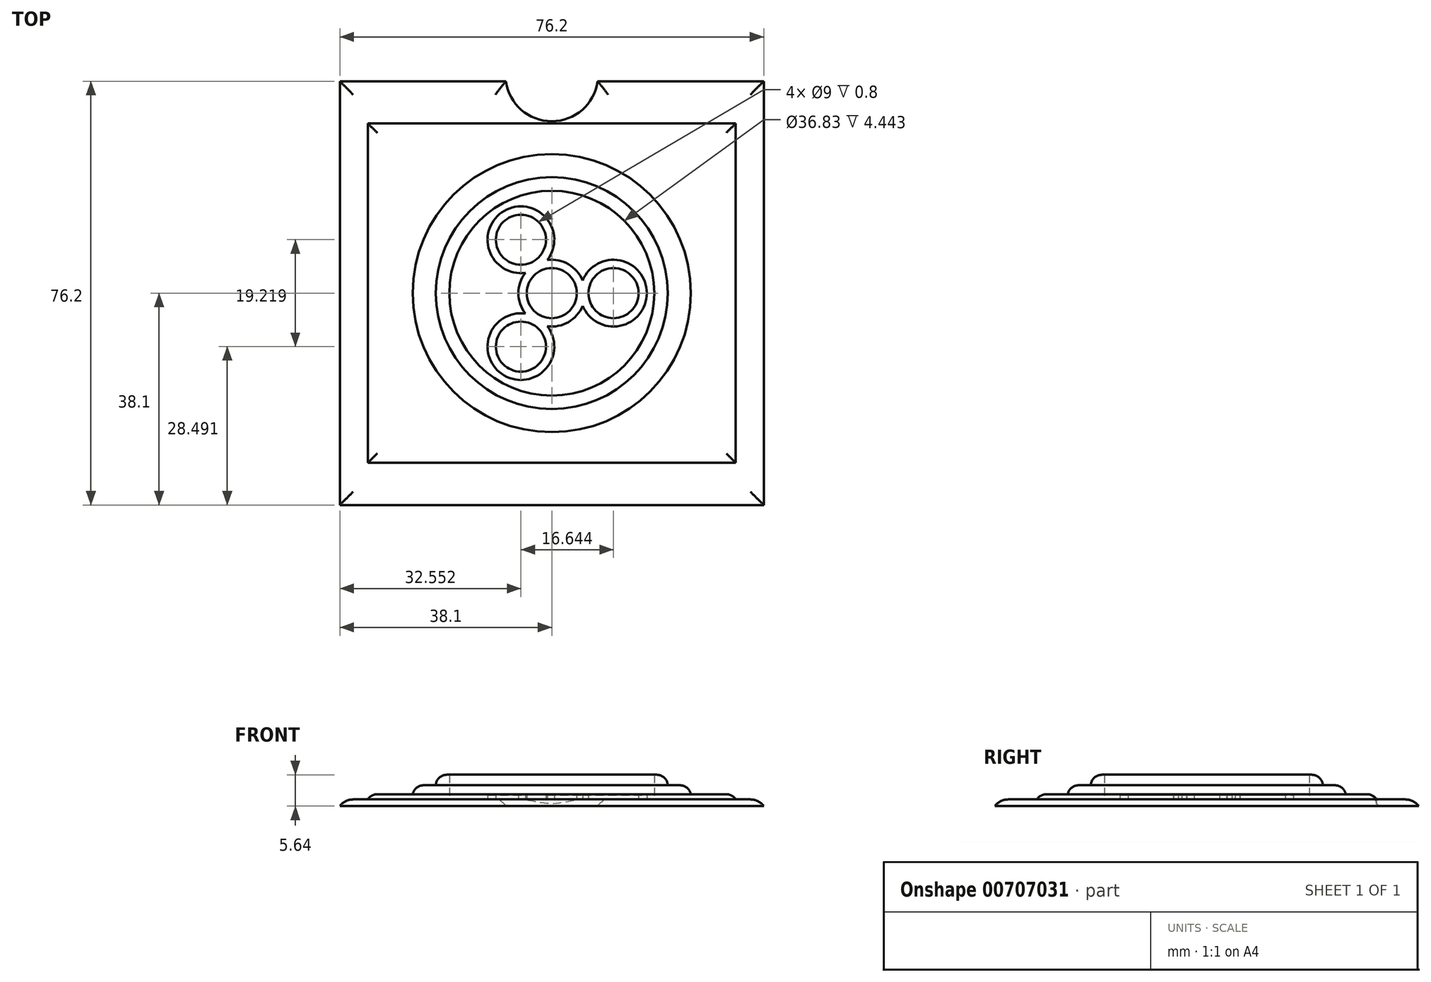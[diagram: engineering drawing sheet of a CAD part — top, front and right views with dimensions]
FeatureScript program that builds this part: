
annotation { "Feature Type Name" : "Feature", "Feature Type Description" : "" }
export const myFeature = defineFeature(function(context is Context, id is Id, definition is map)
    precondition{}
    {
        {
            var Q0;
            Q0=qCreatedBy(makeId("Top.planeOp"),FACE);
            var sketch = newSketch(context, id + "F0", { "sketchPlane" : qUnion([Q0])});
            skLineSegment(sketch, "E0.bottom", {"start": v(38.1, 38.1) * mm, "end": v(-38.1, 38.1) * mm});
            skLineSegment(sketch, "E0.top", {"start": v(38.1, -38.1) * mm, "end": v(-38.1, -38.1) * mm});
            skLineSegment(sketch, "E0.left", {"start": v(38.1, 38.1) * mm, "end": v(38.1, -38.1) * mm});
            skLineSegment(sketch, "E0.right", {"start": v(-38.1, 38.1) * mm, "end": v(-38.1, -38.1) * mm});
            skPoint(sketch, "E0.middle", {"position": v(0, 0) * mm});
            skSolve(sketch);
        }
        {
            var Q0;
            Q0=makeQuery(id+"F0.imprint","IMPRINT",FACE,{"disambiguationData":[TD([[makeQuery(id+"F0.imprint","IMPRINT",EDGE,{"derivedFrom":sQuery(id+"F0.wireOp",EDGE,"E0.bottom")}),1.0]])]});
            extrude(context, id + "F1", {"entities" : qUnion([Q0]), "depth" : 1.2 * mm, "offsetDistance" : 25 * mm});
        }
        {
            var Q0;
            Q0=qCreatedBy(makeId("Top.planeOp"),FACE);
            var sketch = newSketch(context, id + "F2", { "sketchPlane" : qUnion([Q0])});
            skLineSegment(sketch, "E1.bottom", {"start": v(33.07, 30.52) * mm, "end": v(-33.07, 30.52) * mm});
            skLineSegment(sketch, "E1.top", {"start": v(33.07, -30.52) * mm, "end": v(-33.07, -30.52) * mm});
            skLineSegment(sketch, "E1.left", {"start": v(33.07, 30.52) * mm, "end": v(33.07, -30.52) * mm});
            skLineSegment(sketch, "E1.right", {"start": v(-33.07, 30.52) * mm, "end": v(-33.07, -30.52) * mm});
            skPoint(sketch, "E1.middle", {"position": v(0, 0) * mm});
            skSolve(sketch);
        }
        {
            var Q0;
            Q0=makeQuery(id+"F2.imprint","IMPRINT",FACE,{"disambiguationData":[TD([[makeQuery(id+"F2.imprint","IMPRINT",EDGE,{"derivedFrom":sQuery(id+"F2.wireOp",EDGE,"E1.bottom")}),1.0]])]});
            extrude(context, id + "F3", {"entities" : qUnion([Q0]), "operationType" : NewBodyOperationType.ADD, "depth" : 2.14 * mm, "offsetDistance" : 25 * mm});
        }
        {
            var Q0;
            Q0=qCreatedBy(makeId("Top.planeOp"),FACE);
            var sketch = newSketch(context, id + "F4", { "sketchPlane" : qUnion([Q0])});
            skCircle(sketch, "E2", {"center": v(0, 0) * mm, "radius": 25 * mm});
            skSolve(sketch);
        }
        {
            var Q0;
            Q0=makeQuery(id+"F4.imprint","IMPRINT",FACE,{"disambiguationData":[TD([[makeQuery(id+"F4.imprint","IMPRINT",EDGE,{"derivedFrom":sQuery(id+"F4.wireOp",EDGE,"E2")}),1.0]])]});
            extrude(context, id + "F5", {"entities" : qUnion([Q0]), "operationType" : NewBodyOperationType.ADD, "depth" : 3.75 * mm, "offsetDistance" : 25 * mm});
        }
        {
            var Q0;
            Q0=qCreatedBy(makeId("Top.planeOp"),FACE);
            var sketch = newSketch(context, id + "F6", { "sketchPlane" : qUnion([Q0])});
            skCircle(sketch, "E3", {"center": v(0, 0) * mm, "radius": 20.85 * mm});
            skSolve(sketch);
        }
        {
            var Q0;
            Q0=qCreatedBy(makeId("Top.planeOp"),FACE);
            var sketch = newSketch(context, id + "F7", { "sketchPlane" : qUnion([Q0])});
            skCircle(sketch, "E4", {"center": v(0, 0) * mm, "radius": 20.6 * mm});
            skSolve(sketch);
        }
        {
            var Q0;
            Q0=makeQuery(id+"F6.imprint","IMPRINT",FACE,{"disambiguationData":[TD([[makeQuery(id+"F6.imprint","IMPRINT",EDGE,{"derivedFrom":sQuery(id+"F6.wireOp",EDGE,"E3")}),1.0]])]});
            extrude(context, id + "F8", {"entities" : qUnion([Q0]), "operationType" : NewBodyOperationType.ADD, "depth" : 5.64 * mm, "offsetDistance" : 25 * mm});
        }
        {
            var Q0;
            Q0=qCreatedBy(makeId("Top.planeOp"),FACE);
            var sketch = newSketch(context, id + "F9", { "sketchPlane" : qUnion([Q0])});
            skCircle(sketch, "E5", {"center": v(0, 0) * mm, "radius": 18.42 * mm});
            skSolve(sketch);
        }
        {
            var Q0;
            Q0=makeQuery(id+"F9.imprint","IMPRINT",FACE,{"disambiguationData":[TD([[makeQuery(id+"F9.imprint","IMPRINT",EDGE,{"derivedFrom":sQuery(id+"F9.wireOp",EDGE,"E5")}),1.0]])]});
            extrude(context, id + "F10", {"entities" : qUnion([Q0]), "operationType" : NewBodyOperationType.REMOVE, "depth" : 6 * mm, "offsetDistance" : 25 * mm});
        }
        {
            var Q0;
            Q0=makeQuery(id+"F7.imprint","IMPRINT",FACE,{"disambiguationData":[TD([[makeQuery(id+"F7.imprint","IMPRINT",EDGE,{"derivedFrom":sQuery(id+"F7.wireOp",EDGE,"E4")}),1.0]])]});
            extrude(context, id + "F11", {"entities" : qUnion([Q0]), "operationType" : NewBodyOperationType.ADD, "depth" : 1.2 * mm, "offsetDistance" : 25 * mm});
        }
        {
            var Q0;
            Q0=qCreatedBy(makeId("Top.planeOp"),FACE);
            var sketch = newSketch(context, id + "F12", { "sketchPlane" : qUnion([Q0])});
            skCircle(sketch, "E6", {"center": v(0, 0) * mm, "radius": 6 * mm});
            skCircle(sketch, "E7", {"center": v(11.1, 0) * mm, "radius": 6 * mm});
            skCircle(sketch, "E8.1.0", {"center": v(-5.55, 9.6) * mm, "radius": 6 * mm});
            skCircle(sketch, "E8.2.0", {"center": v(-5.55, -9.6) * mm, "radius": 6 * mm});
            skCircle(sketch, "E9", {"center": v(11.1, 0) * mm, "radius": 4.5 * mm});
            skCircle(sketch, "E10", {"center": v(-5.55, 9.6) * mm, "radius": 4.5 * mm});
            skCircle(sketch, "E11", {"center": v(-5.55, -9.6) * mm, "radius": 4.5 * mm});
            skCircle(sketch, "E12", {"center": v(0, 0) * mm, "radius": 4.5 * mm});
            skSolve(sketch);
        }
        {
            var Q0;
            {var subQ0=sQuery(id+"F12.wireOp",EDGE,"E8.1.0");var subQ1=sQuery(id+"F12.wireOp",EDGE,"E6");var subQ2=makeQuery(id+"F12.imprint","INTERSECT",VERTEX,{"disambiguationData":[OD(0.0)],"derivedFrom":[subQ1,subQ0]});Q0=makeQuery(id+"F12.imprint","IMPRINT",FACE,{"disambiguationData":[TD([[makeQuery(id+"F12.imprint","IMPRINT",EDGE,{"disambiguationData":[TD([[subQ2,-1.0]])],"derivedFrom":subQ1}),-1.0]])]});}
            var Q1;
            {var subQ1=sQuery(id+"F12.wireOp",EDGE,"E6");var subQ6=sQuery(id+"F12.wireOp",EDGE,"E8.1.0");var subQ9=makeQuery(id+"F12.imprint","INTERSECT",VERTEX,{"disambiguationData":[OD(0.0)],"derivedFrom":[subQ1,subQ6]});Q1=makeQuery(id+"F12.imprint","IMPRINT",FACE,{"disambiguationData":[TD([[makeQuery(id+"F12.imprint","IMPRINT",EDGE,{"disambiguationData":[TD([[subQ9,1.0]])],"derivedFrom":subQ1}),1.0]])]});}
            var Q2;
            {var subQ0=sQuery(id+"F12.wireOp",EDGE,"E7");var subQ1=sQuery(id+"F12.wireOp",EDGE,"E6");var subQ2=makeQuery(id+"F12.imprint","INTERSECT",VERTEX,{"disambiguationData":[OD(0.0)],"derivedFrom":[subQ1,subQ0]});Q2=makeQuery(id+"F12.imprint","IMPRINT",FACE,{"disambiguationData":[TD([[makeQuery(id+"F12.imprint","IMPRINT",EDGE,{"disambiguationData":[TD([[subQ2,1.0]])],"derivedFrom":subQ1}),-1.0]])]});}
            var Q3;
            {var subQ0=sQuery(id+"F12.wireOp",EDGE,"E8.2.0");var subQ1=sQuery(id+"F12.wireOp",EDGE,"E6");var subQ2=makeQuery(id+"F12.imprint","INTERSECT",VERTEX,{"disambiguationData":[OD(0.0)],"derivedFrom":[subQ1,subQ0]});Q3=makeQuery(id+"F12.imprint","IMPRINT",FACE,{"disambiguationData":[TD([[makeQuery(id+"F12.imprint","IMPRINT",EDGE,{"disambiguationData":[TD([[subQ2,-1.0]])],"derivedFrom":subQ1}),-1.0]])]});}
            var Q4;
            {var subQ0=sQuery(id+"F12.wireOp",EDGE,"E8.1.0");var subQ1=sQuery(id+"F12.wireOp",EDGE,"E6");var subQ2=makeQuery(id+"F12.imprint","INTERSECT",VERTEX,{"disambiguationData":[OD(0.0)],"derivedFrom":[subQ1,subQ0]});Q4=makeQuery(id+"F12.imprint","IMPRINT",FACE,{"disambiguationData":[TD([[makeQuery(id+"F12.imprint","IMPRINT",EDGE,{"disambiguationData":[TD([[subQ2,-1.0]])],"derivedFrom":subQ1}),1.0]])]});}
            var Q5;
            {var subQ0=sQuery(id+"F12.wireOp",EDGE,"E7");var subQ1=sQuery(id+"F12.wireOp",EDGE,"E6");var subQ2=makeQuery(id+"F12.imprint","INTERSECT",VERTEX,{"disambiguationData":[OD(0.0)],"derivedFrom":[subQ1,subQ0]});Q5=makeQuery(id+"F12.imprint","IMPRINT",FACE,{"disambiguationData":[TD([[makeQuery(id+"F12.imprint","IMPRINT",EDGE,{"disambiguationData":[TD([[subQ2,1.0]])],"derivedFrom":subQ1}),1.0]])]});}
            var Q6;
            {var subQ0=sQuery(id+"F12.wireOp",EDGE,"E8.2.0");var subQ1=sQuery(id+"F12.wireOp",EDGE,"E6");var subQ2=makeQuery(id+"F12.imprint","INTERSECT",VERTEX,{"disambiguationData":[OD(0.0)],"derivedFrom":[subQ1,subQ0]});Q6=makeQuery(id+"F12.imprint","IMPRINT",FACE,{"disambiguationData":[TD([[makeQuery(id+"F12.imprint","IMPRINT",EDGE,{"disambiguationData":[TD([[subQ2,-1.0]])],"derivedFrom":subQ1}),1.0]])]});}
            extrude(context, id + "F13", {"entities" : qUnion([Q0, Q1, Q2, Q3, Q4, Q5, Q6]), "operationType" : NewBodyOperationType.ADD, "depth" : 2 * mm, "offsetDistance" : 25 * mm});
        }
        {
            var Q0;
            Q0=qCreatedBy(makeId("Top.planeOp"),FACE);
            var sketch = newSketch(context, id + "F14", { "sketchPlane" : qUnion([Q0])});
            skCircle(sketch, "E13", {"center": v(0, 39.23) * mm, "radius": 8.32 * mm});
            skSolve(sketch);
        }
        {
            var Q0;
            Q0=makeQuery(id+"F14.imprint","IMPRINT",FACE,{"disambiguationData":[TD([[makeQuery(id+"F14.imprint","IMPRINT",EDGE,{"derivedFrom":sQuery(id+"F14.wireOp",EDGE,"E13")}),1.0]])]});
            extrude(context, id + "F15", {"entities" : qUnion([Q0]), "operationType" : NewBodyOperationType.REMOVE, "depth" : 3 * mm, "offsetDistance" : 25 * mm});
        }
        {
            var Q0;
            {var subQ0=sQuery(id+"F0.wireOp",EDGE,"E0.bottom");var subQ1=sQuery(id+"F0.wireOp",EDGE,"E0.right");Q0=makeQuery(id+"F15.boolean.opBoolean","SPLIT",EDGE,{"disambiguationData":[TD([makeQuery(id+"F1.opExtrude","SWEPT_FACE",FACE,{"disambiguationData":[OSD([subQ1])]})])],"derivedFrom":makeQuery(id+"F1.opExtrude","CAP_EDGE",EDGE,{"disambiguationData":[OSD([subQ0])],"isStart":false})});}
            var Q1;
            Q1=makeQuery(id+"F15.boolean.opBoolean","INTERSECT",EDGE,{"derivedFrom":[makeQuery(id+"F1.opExtrude","CAP_FACE",FACE,{"disambiguationData":[OSD([sQuery(id+"F0.wireOp",EDGE,"E0.bottom"),sQuery(id+"F0.wireOp",EDGE,"E0.top"),sQuery(id+"F0.wireOp",EDGE,"E0.left"),sQuery(id+"F0.wireOp",EDGE,"E0.right")])],"isStart":false}),makeQuery(id+"F15.opExtrude","SWEPT_FACE",FACE,{"disambiguationData":[OSD([sQuery(id+"F14.wireOp",EDGE,"E13")])]})]});
            var Q2;
            {var subQ0=sQuery(id+"F0.wireOp",EDGE,"E0.bottom");var subQ1=sQuery(id+"F0.wireOp",EDGE,"E0.left");Q2=makeQuery(id+"F15.boolean.opBoolean","SPLIT",EDGE,{"disambiguationData":[TD([makeQuery(id+"F1.opExtrude","SWEPT_FACE",FACE,{"disambiguationData":[OSD([subQ1])]})])],"derivedFrom":makeQuery(id+"F1.opExtrude","CAP_EDGE",EDGE,{"disambiguationData":[OSD([subQ0])],"isStart":false})});}
            var Q3;
            Q3=makeQuery(id+"F1.opExtrude","CAP_EDGE",EDGE,{"disambiguationData":[OSD([sQuery(id+"F0.wireOp",EDGE,"E0.left")])],"isStart":false});
            var Q4;
            Q4=makeQuery(id+"F1.opExtrude","CAP_EDGE",EDGE,{"disambiguationData":[OSD([sQuery(id+"F0.wireOp",EDGE,"E0.top")])],"isStart":false});
            var Q5;
            Q5=makeQuery(id+"F1.opExtrude","CAP_EDGE",EDGE,{"disambiguationData":[OSD([sQuery(id+"F0.wireOp",EDGE,"E0.right")])],"isStart":false});
            fillet(context, id + "F16", {"entities" : qUnion([Q0, Q1, Q2, Q3, Q4, Q5]), "radius" : 3 * mm, "tangentPropagation" : true, "allowEdgeOverflow" : false});
        }
        {
            var Q0;
            Q0=makeQuery(id+"F3.opExtrude","CAP_EDGE",EDGE,{"disambiguationData":[OSD([sQuery(id+"F2.wireOp",EDGE,"E1.bottom")])],"isStart":false});
            var Q1;
            Q1=makeQuery(id+"F3.opExtrude","CAP_EDGE",EDGE,{"disambiguationData":[OSD([sQuery(id+"F2.wireOp",EDGE,"E1.right")])],"isStart":false});
            var Q2;
            Q2=makeQuery(id+"F3.opExtrude","CAP_EDGE",EDGE,{"disambiguationData":[OSD([sQuery(id+"F2.wireOp",EDGE,"E1.left")])],"isStart":false});
            var Q3;
            Q3=makeQuery(id+"F3.opExtrude","CAP_EDGE",EDGE,{"disambiguationData":[OSD([sQuery(id+"F2.wireOp",EDGE,"E1.top")])],"isStart":false});
            var Q4;
            Q4=makeQuery(id+"F5.opExtrude","CAP_EDGE",EDGE,{"disambiguationData":[OSD([sQuery(id+"F4.wireOp",EDGE,"E2")])],"isStart":false});
            var Q5;
            Q5=makeQuery(id+"F8.opExtrude","CAP_EDGE",EDGE,{"disambiguationData":[OSD([sQuery(id+"F6.wireOp",EDGE,"E3")])],"isStart":false});
            fillet(context, id + "F17", {"entities" : qUnion([Q0, Q1, Q2, Q3, Q4, Q5]), "radius" : 2 * mm, "tangentPropagation" : true, "allowEdgeOverflow" : false});
        }
    });
